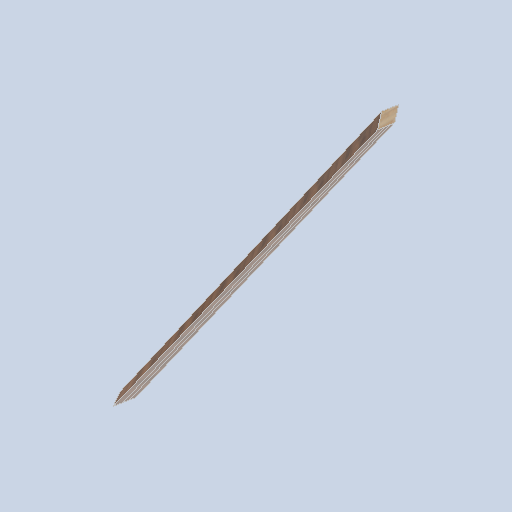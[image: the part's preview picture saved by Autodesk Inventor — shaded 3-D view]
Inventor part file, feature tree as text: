
AUTODESK INVENTOR PART (.ipt)
format: ipt  version: 2024.2 (Build 282272000, 272)  size: 300,032 bytes
history: native  units: mm
features: sketch x4, plane x2, loft x1
ambient origin geometry x8: Origin, YZ Plane, XZ Plane, XY Plane, X Axis, Y Axis, Z Axis, Center Point
bodies: Solid1 (feature_tree)
feature tree (7):
  sketch  "Sketch1"  dims[d0=0.0mm d1=1791.0mm d2=0.0mm d3=90.0deg]
  plane  "Work Plane2"
  loft  "Loft1"
  sketch  "Sketch4"
  plane  "Work Plane1"
  sketch  "Sketch2"  dims[d4=0.0mm d5=90.0deg]
  sketch  "Sketch3"
